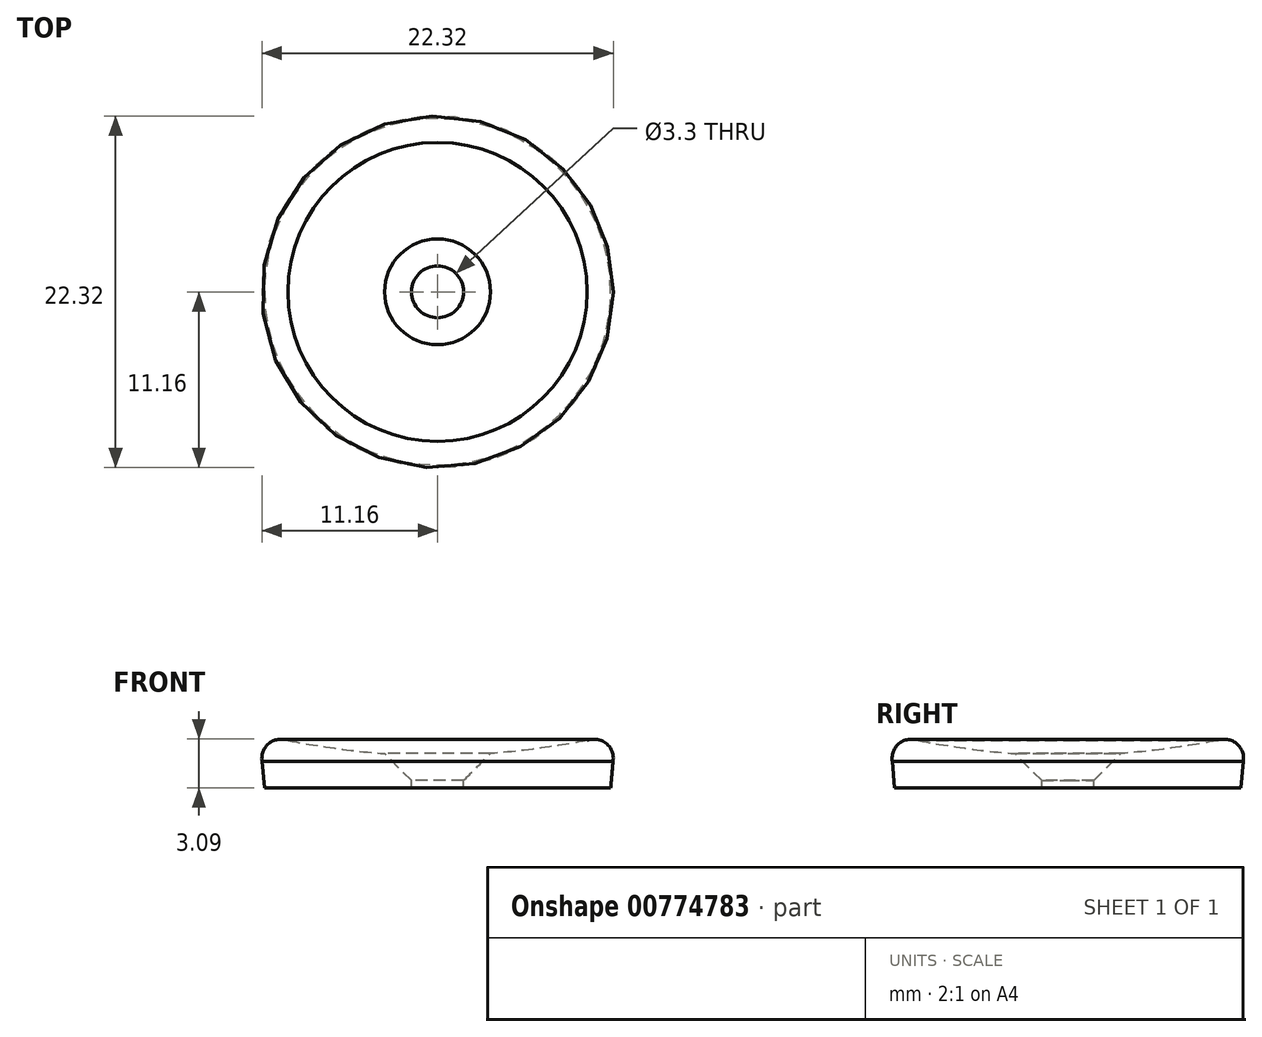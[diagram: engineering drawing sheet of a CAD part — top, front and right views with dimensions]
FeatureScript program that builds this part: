
annotation { "Feature Type Name" : "Feature", "Feature Type Description" : "" }
export const myFeature = defineFeature(function(context is Context, id is Id, definition is map)
    precondition{}
    {
        {
            var Q0;
            Q0=qCreatedBy(makeId("Front.planeOp"),FACE);
            var sketch = newSketch(context, id + "F0", { "sketchPlane" : qUnion([Q0])});
            skLineSegment(sketch, "E0.bottom", {"start": v(0, 0) * mm, "end": v(-11, 0) * mm});
            skArc(sketch, "E1", {"start": v(-9.5, 3) * mm, "mid": v(-10.71, 2.81) * mm, "end": v(-11.15, 1.66) * mm});
            skArc(sketch, "E2", {"start": v(-9.5, 3) * mm, "mid": v(-4.77, 2.3) * mm, "end": v(0, 2) * mm});
            skLineSegment(sketch, "E3", {"start": v(0, 2) * mm, "end": v(0, 0) * mm});
            skLineSegment(sketch, "E4", {"start": v(-11.15, 1.66) * mm, "end": v(-11, 0) * mm});
            skSolve(sketch);
        }
        {
            var Q0;
            Q0 = qSketchRegion(id + "F0", true);
            var Q1;
            Q1=sQuery(id+"F0.wireOp",EDGE,"E3");
            revolve(context, id + "F1", {"surfaceOperationType" : NewSurfaceOperationType.NEW, "entities" : qUnion([Q0]), "axis" : qUnion([Q1]), "revolveType" : RevolveType.FULL});
        }
        {
            var Q0;
            Q0=qCreatedBy(makeId("Top.planeOp"),FACE);
            cPlane(context, id + "F2", {"entities" : qUnion([Q0]), "cplaneType" : CPlaneType.OFFSET, "offset" : 2.27 * mm, "width" : 150 * mm, "height" : 150 * mm});
        }
        {
            var Q0;
            Q0=qCreatedBy(id+"F2.planeOp",FACE);
            var sketch = newSketch(context, id + "F3", { "sketchPlane" : qUnion([Q0])});
            skPoint(sketch, "E5", {"position": v(0, 0) * mm});
            skSolve(sketch);
        }
        {
            var Q0;
            Q0=sQuery(id+"F3.wireOp",VERTEX,"E5");
            var Q1;
            Q1=makeQuery(id+"F1.opRevolve","SWEPT_BODY",BODY,{"disambiguationData":[OSD([sQuery(id+"F0.wireOp",EDGE,"E0.bottom"),sQuery(id+"F0.wireOp",EDGE,"E1"),sQuery(id+"F0.wireOp",EDGE,"E2"),sQuery(id+"F0.wireOp",EDGE,"E3"),sQuery(id+"F0.wireOp",EDGE,"E4")])]});
            hole(context, id + "F4", {"style" : HoleStyle.C_SINK, "endStyle" : HoleEndStyle.THROUGH, "standardTappedOrClearance" : lookupTablePath({ "standard" : "ISO", "fit" : "Normal", "size" : "M3", "type" : "Clearance" }), "standardBlindInLast" : lookupTablePath({ "fit" : "Standard", "standard" : "ISO", "size" : "M3", "type" : "Clearance" }), "holeDiameter" : 3.3 * mm, "cSinkDiameter" : 6.72 * mm, "cSinkAngle" : 90 * degree, "majorDiameter" : 5 * mm, "isTappedThrough" : true, "tappedDepth" : 12 * mm, "tapClearance" : 3, "locations" : qUnion([Q0]), "scope" : qUnion([Q1])});
        }
    });
